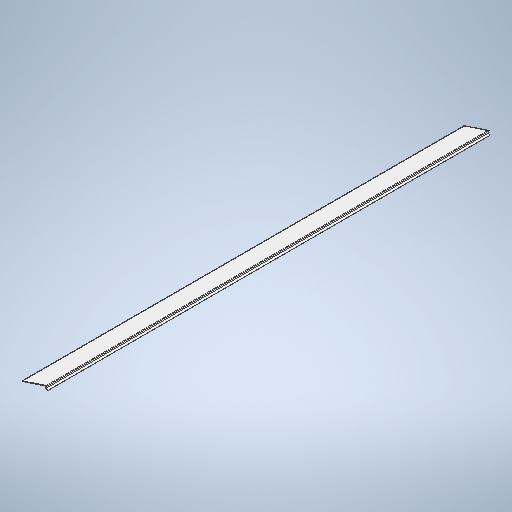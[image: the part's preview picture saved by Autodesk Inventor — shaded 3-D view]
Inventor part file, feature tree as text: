
AUTODESK INVENTOR PART (.ipt)
format: ipt  version: 2025 (Build 290162010, 162A)  size: 293,376 bytes
history: native  units: in
note: dims shown in document units (in); Inventor stores cm internally (conversion verified against a paired STEP export)
features: extrude x1, sketch x1
ambient origin geometry x8: Origin, YZ Plane, XZ Plane, XY Plane, X Axis, Y Axis, Z Axis, Center Point
bodies: Body1 (feature_tree)
feature tree (2):
  extrude  "Extrusion2"  Depth=0.125in
  sketch  "Sketch1"  dims[d5=5.5in d17=3.5in d19=132.0in d23=1.194in d28=1.8188in d33=42.875in d36=1.0in d37=0.625in d49=0.125in d50=0.125in d51=0.125in d52=0.125in d54=0.333in d55=0.333in d59=97.837in d60=0.0in d61=0.333in d62=6.0in d63=0.125in d65=0.5in d73=6.0in d74=0.5in d75=0.125in d76=0.125in d78=0.333in d79=0.333in d80=0.333in]
